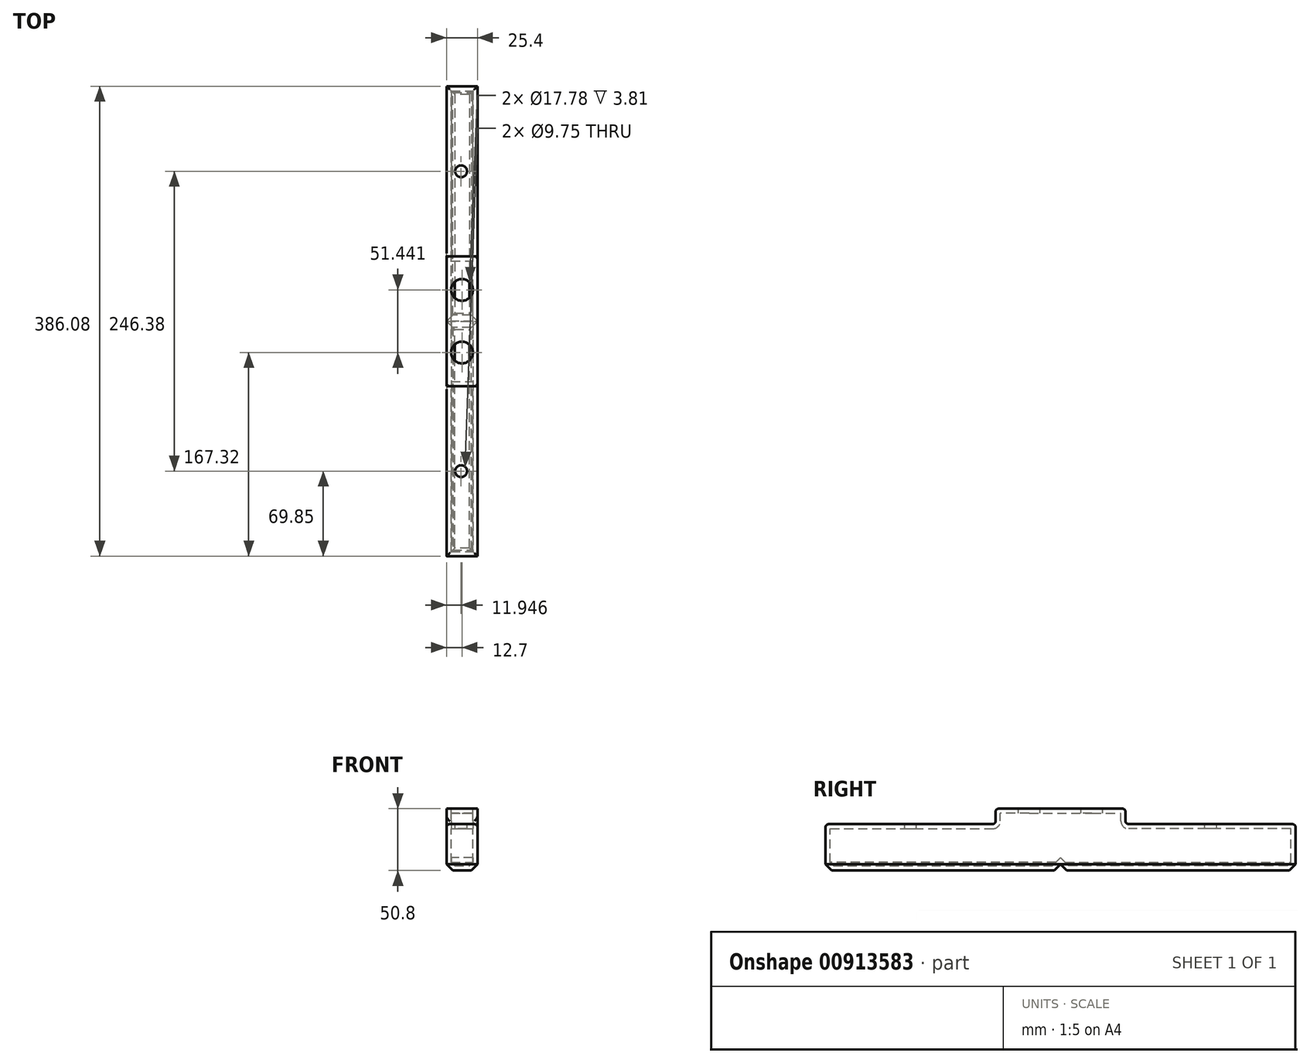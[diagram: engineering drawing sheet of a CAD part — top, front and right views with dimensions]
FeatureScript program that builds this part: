
annotation { "Feature Type Name" : "Feature", "Feature Type Description" : "" }
export const myFeature = defineFeature(function(context is Context, id is Id, definition is map)
    precondition{}
    {
        {
            var Q0;
            Q0=qCreatedBy(makeId("Right.planeOp"),FACE);
            var sketch = newSketch(context, id + "F0", { "sketchPlane" : qUnion([Q0])});
            skLineSegment(sketch, "E0", {"start": v(-243.84, 60.41) * mm, "end": v(-243.84, 9.61) * mm});
            skLineSegment(sketch, "E1", {"start": v(-243.84, 9.61) * mm, "end": v(-50.8, 9.61) * mm});
            skLineSegment(sketch, "E2", {"start": v(-50.8, 9.61) * mm, "end": v(-50.8, 47.71) * mm});
            skLineSegment(sketch, "E3", {"start": v(-50.8, 47.71) * mm, "end": v(-190.5, 47.71) * mm});
            skLineSegment(sketch, "E4", {"start": v(-190.5, 47.71) * mm, "end": v(-190.5, 60.41) * mm});
            skLineSegment(sketch, "E5", {"start": v(-243.84, 60.41) * mm, "end": v(-190.5, 60.41) * mm});
            skSolve(sketch);
        }
        {
            var Q0;
            Q0=makeQuery(id+"F0.imprint","IMPRINT",FACE,{"disambiguationData":[TD([[makeQuery(id+"F0.imprint","IMPRINT",EDGE,{"derivedFrom":sQuery(id+"F0.wireOp",EDGE,"E0")}),1.0]])]});
            extrude(context, id + "F1", {"entities" : qUnion([Q0]), "depth" : 25.4 * mm, "offsetDistance" : 25.4 * mm});
        }
        {
            var Q0;
            Q0=makeQuery(id+"F1.opExtrude","SWEPT_EDGE",EDGE,{"disambiguationData":[OSD([sQuery(id+"F0.wireOp",EDGE,"E3"),sQuery(id+"F0.wireOp",EDGE,"E4")])]});
            var Q1;
            Q1=makeQuery(id+"F1.opExtrude","CAP_EDGE",EDGE,{"disambiguationData":[OSD([sQuery(id+"F0.wireOp",EDGE,"E3")])],"isStart":false});
            var Q2;
            Q2=makeQuery(id+"F1.opExtrude","CAP_EDGE",EDGE,{"disambiguationData":[OSD([sQuery(id+"F0.wireOp",EDGE,"E3")])],"isStart":true});
            var Q3;
            Q3=makeQuery(id+"F1.opExtrude","SWEPT_EDGE",EDGE,{"disambiguationData":[OSD([sQuery(id+"F0.wireOp",EDGE,"E2"),sQuery(id+"F0.wireOp",EDGE,"E3")])]});
            var Q4;
            Q4=makeQuery(id+"F1.opExtrude","SWEPT_EDGE",EDGE,{"disambiguationData":[OSD([sQuery(id+"F0.wireOp",EDGE,"E4"),sQuery(id+"F0.wireOp",EDGE,"E5")])]});
            fillet(context, id + "F2", {"entities" : qUnion([Q0, Q1, Q2, Q3, Q4]), "radius" : 2.54 * mm, "tangentPropagation" : true, "allowEdgeOverflow" : false});
        }
        {
            var Q0;
            Q0=makeQuery(id+"F1.opExtrude","CAP_EDGE",EDGE,{"disambiguationData":[OSD([sQuery(id+"F0.wireOp",EDGE,"E1")])],"isStart":false});
            var Q1;
            Q1=makeQuery(id+"F1.opExtrude","SWEPT_FACE",FACE,{"disambiguationData":[OSD([sQuery(id+"F0.wireOp",EDGE,"E1")])]});
            chamfer(context, id + "F3", {"entities" : qUnion([Q0, Q1]), "width" : 5.08 * mm, "tangentPropagation" : true});
        }
        {
            var Q0;
            Q0=makeQuery(id+"F1.opExtrude","SWEPT_FACE",FACE,{"disambiguationData":[OSD([sQuery(id+"F0.wireOp",EDGE,"E0")])]});
            shell(context, id + "F4", {"entities" : qUnion([Q0]), "thickness" : 3.8 * mm});
        }
        {
            var Q0;
            Q0=makeQuery(id+"F1.opExtrude","SWEPT_FACE",FACE,{"disambiguationData":[OSD([sQuery(id+"F0.wireOp",EDGE,"E5")])]});
            var sketch = newSketch(context, id + "F5", { "sketchPlane" : qUnion([Q0])});
            skCircle(sketch, "E6", {"center": v(12.7, -218.12) * mm, "radius": 8.9 * mm});
            skPoint(sketch, "E7", {"position": v(11.95, -120.65) * mm});
            skLineSegment(sketch, "E8", {"start": v(-21.44, -120.65) * mm, "end": v(-4.47, -120.65) * mm, "construction": true});
            skLineSegment(sketch, "E9", {"start": v(-4.47, -120.65) * mm, "end": v(-8.02, -120.65) * mm, "construction": true});
            skSolve(sketch);
        }
        {
            var Q0;
            Q0=makeQuery(id+"F5.imprint","IMPRINT",FACE,{"disambiguationData":[TD([[makeQuery(id+"F5.imprint","IMPRINT",EDGE,{"derivedFrom":sQuery(id+"F5.wireOp",EDGE,"E6")}),1.0]])]});
            var Q1;
            Q1=makeQuery(id+"F4.opShell","OFFSET_FACE",FACE,{"disambiguationData":[OSD([sQuery(id+"F0.wireOp",EDGE,"E5")])]});
            extrude(context, id + "F6", {"entities" : qUnion([Q0]), "operationType" : NewBodyOperationType.REMOVE, "endBound" : BoundingType.UP_TO_SURFACE, "oppositeDirection" : true, "depth" : 26.42 * mm, "endBoundEntityFace" : qUnion([Q1]), "offsetDistance" : 25.4 * mm});
        }
        {
            var Q0;
            Q0=sQuery(id+"F5.wireOp",VERTEX,"E7");
            var Q1;
            Q1=makeQuery(id+"F1.opExtrude","SWEPT_BODY",BODY,{"disambiguationData":[OSD([sQuery(id+"F0.wireOp",EDGE,"E0"),sQuery(id+"F0.wireOp",EDGE,"E1"),sQuery(id+"F0.wireOp",EDGE,"E2"),sQuery(id+"F0.wireOp",EDGE,"E3"),sQuery(id+"F0.wireOp",EDGE,"E4"),sQuery(id+"F0.wireOp",EDGE,"E5")])]});
            hole(context, id + "F7", {"style" : HoleStyle.C_BORE, "endStyle" : HoleEndStyle.BLIND, "holeDiameter" : 5.5 * mm, "cBoreDiameter" : 9.75 * mm, "cBoreDepth" : 5 * mm, "majorDiameter" : 6.35 * mm, "holeDepth" : 12.7 * mm, "isTappedThrough" : true, "tappedDepth" : 12.7 * mm, "tapClearance" : 3, "locations" : qUnion([Q0]), "scope" : qUnion([Q1])});
        }
        {
            var Q0;
            Q0=makeQuery(id+"F1.opExtrude","SWEPT_BODY",BODY,{"disambiguationData":[OSD([sQuery(id+"F0.wireOp",EDGE,"E0"),sQuery(id+"F0.wireOp",EDGE,"E1"),sQuery(id+"F0.wireOp",EDGE,"E2"),sQuery(id+"F0.wireOp",EDGE,"E3"),sQuery(id+"F0.wireOp",EDGE,"E4"),sQuery(id+"F0.wireOp",EDGE,"E5")])]});
            var Q1;
            Q1=makeQuery(id+"F1.opExtrude","SWEPT_FACE",FACE,{"disambiguationData":[OSD([sQuery(id+"F0.wireOp",EDGE,"E0")])]});
            mirror(context, id + "F8", {"operationType" : NewBodyOperationType.ADD, "entities" : qUnion([Q0]), "mirrorPlane" : qUnion([Q1])});
        }
    });
